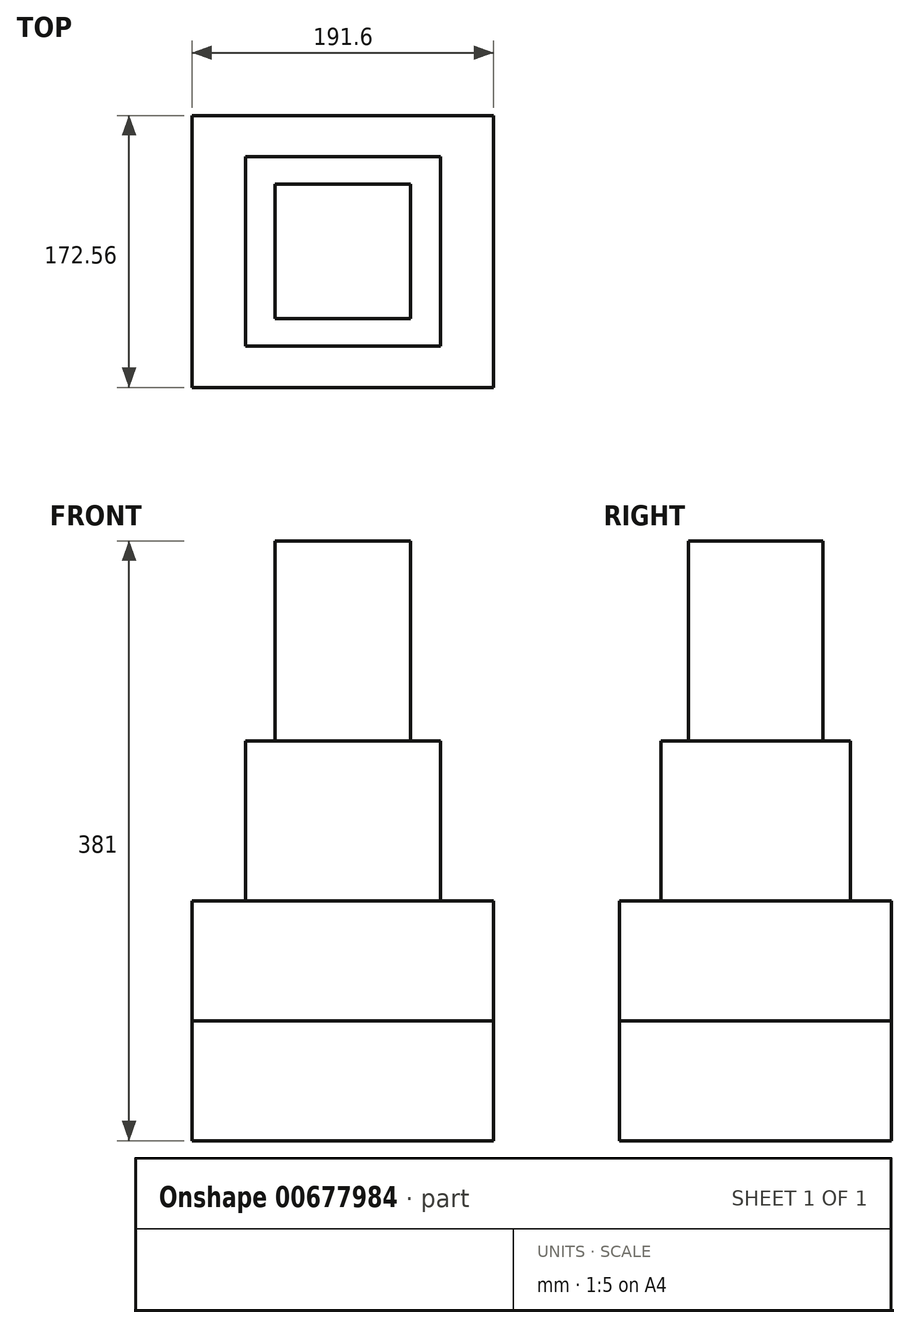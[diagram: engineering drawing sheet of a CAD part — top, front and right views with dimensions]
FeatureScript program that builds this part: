
annotation { "Feature Type Name" : "Feature", "Feature Type Description" : "" }
export const myFeature = defineFeature(function(context is Context, id is Id, definition is map)
    precondition{}
    {
        {
            var Q0;
            Q0=qCreatedBy(makeId("Top.planeOp"),FACE);
            var sketch = newSketch(context, id + "F0", { "sketchPlane" : qUnion([Q0])});
            skLineSegment(sketch, "E0.bottom", {"start": v(-61.84, 60.22) * mm, "end": v(61.84, 60.22) * mm});
            skLineSegment(sketch, "E0.top", {"start": v(-61.84, -60.22) * mm, "end": v(61.84, -60.22) * mm});
            skLineSegment(sketch, "E0.left", {"start": v(-61.84, 60.22) * mm, "end": v(-61.84, -60.22) * mm});
            skLineSegment(sketch, "E0.right", {"start": v(61.84, 60.22) * mm, "end": v(61.84, -60.22) * mm});
            skPoint(sketch, "E0.middle", {"position": v(0, 0) * mm});
            skSolve(sketch);
        }
        {
            var Q0;
            Q0=makeQuery(id+"F0.imprint","IMPRINT",FACE,{"disambiguationData":[TD([[makeQuery(id+"F0.imprint","IMPRINT",EDGE,{"derivedFrom":sQuery(id+"F0.wireOp",EDGE,"E0.bottom")}),-1.0]])]});
            extrude(context, id + "F1", {"entities" : qUnion([Q0]), "depth" : 177.8 * mm, "offsetDistance" : 25.4 * mm});
        }
        {
            var Q0;
            Q0=makeQuery(id+"F1.opExtrude","CAP_FACE",FACE,{"disambiguationData":[OSD([sQuery(id+"F0.wireOp",EDGE,"E0.bottom"),sQuery(id+"F0.wireOp",EDGE,"E0.top"),sQuery(id+"F0.wireOp",EDGE,"E0.left"),sQuery(id+"F0.wireOp",EDGE,"E0.right")])],"isStart":false});
            var sketch = newSketch(context, id + "F2", { "sketchPlane" : qUnion([Q0])});
            skLineSegment(sketch, "E1.bottom", {"start": v(-42.93, 42.71) * mm, "end": v(42.93, 42.71) * mm});
            skLineSegment(sketch, "E1.top", {"start": v(-42.93, -42.71) * mm, "end": v(42.93, -42.71) * mm});
            skLineSegment(sketch, "E1.left", {"start": v(-42.93, 42.71) * mm, "end": v(-42.93, -42.71) * mm});
            skLineSegment(sketch, "E1.right", {"start": v(42.93, 42.71) * mm, "end": v(42.93, -42.71) * mm});
            skPoint(sketch, "E1.middle", {"position": v(0, 0) * mm});
            skSolve(sketch);
        }
        {
            var Q0;
            Q0 = qSketchRegion(id + "F2", true);
            extrude(context, id + "F3", {"entities" : qUnion([Q0]), "operationType" : NewBodyOperationType.ADD, "depth" : 127 * mm, "offsetDistance" : 25.4 * mm});
        }
        {
            var Q0;
            Q0=makeQuery(id+"F0.imprint","IMPRINT",FACE,{"disambiguationData":[TD([[makeQuery(id+"F0.imprint","IMPRINT",EDGE,{"derivedFrom":sQuery(id+"F0.wireOp",EDGE,"E0.bottom")}),-1.0]])]});
            var sketch = newSketch(context, id + "F4", { "sketchPlane" : qUnion([Q0])});
            skLineSegment(sketch, "E2.bottom", {"start": v(-95.8, -86.28) * mm, "end": v(95.8, -86.28) * mm});
            skLineSegment(sketch, "E2.top", {"start": v(-95.8, 86.28) * mm, "end": v(95.8, 86.28) * mm});
            skLineSegment(sketch, "E2.left", {"start": v(-95.8, -86.28) * mm, "end": v(-95.8, 86.28) * mm});
            skLineSegment(sketch, "E2.right", {"start": v(95.8, -86.28) * mm, "end": v(95.8, 86.28) * mm});
            skPoint(sketch, "E2.middle", {"position": v(0, 0) * mm});
            skSolve(sketch);
        }
        {
            var Q0;
            Q0 = qSketchRegion(id + "F4", true);
            extrude(context, id + "F5", {"entities" : qUnion([Q0]), "operationType" : NewBodyOperationType.ADD, "depth" : 76.2 * mm, "offsetDistance" : 25.4 * mm});
        }
        {
            var Q0;
            Q0=makeQuery(id+"F5.boolean.opBoolean","MERGE",FACE,{"derivedFrom":[makeQuery(id+"F1.opExtrude","CAP_FACE",FACE,{"disambiguationData":[OSD([sQuery(id+"F0.wireOp",EDGE,"E0.bottom"),sQuery(id+"F0.wireOp",EDGE,"E0.top"),sQuery(id+"F0.wireOp",EDGE,"E0.left"),sQuery(id+"F0.wireOp",EDGE,"E0.right")])],"isStart":true}),makeQuery(id+"F5.opExtrude","CAP_FACE",FACE,{"disambiguationData":[OSD([sQuery(id+"F4.wireOp",EDGE,"E2.bottom"),sQuery(id+"F4.wireOp",EDGE,"E2.top"),sQuery(id+"F4.wireOp",EDGE,"E2.left"),sQuery(id+"F4.wireOp",EDGE,"E2.right")])],"isStart":true})]});
            var sketch = newSketch(context, id + "F6", { "sketchPlane" : qUnion([Q0])});
            skLineSegment(sketch, "E3.bottom", {"start": v(-95.8, 86.28) * mm, "end": v(95.8, 86.28) * mm});
            skLineSegment(sketch, "E3.top", {"start": v(-95.8, -86.28) * mm, "end": v(95.8, -86.28) * mm});
            skLineSegment(sketch, "E3.left", {"start": v(-95.8, 86.28) * mm, "end": v(-95.8, -86.28) * mm});
            skLineSegment(sketch, "E3.right", {"start": v(95.8, 86.28) * mm, "end": v(95.8, -86.28) * mm});
            skPoint(sketch, "E3.middle", {"position": v(0, 0) * mm});
            skSolve(sketch);
        }
        {
            var Q0;
            Q0 = qSketchRegion(id + "F6", true);
            extrude(context, id + "F7", {"entities" : qUnion([Q0]), "depth" : 76.2 * mm, "offsetDistance" : 25.4 * mm});
        }
    });
